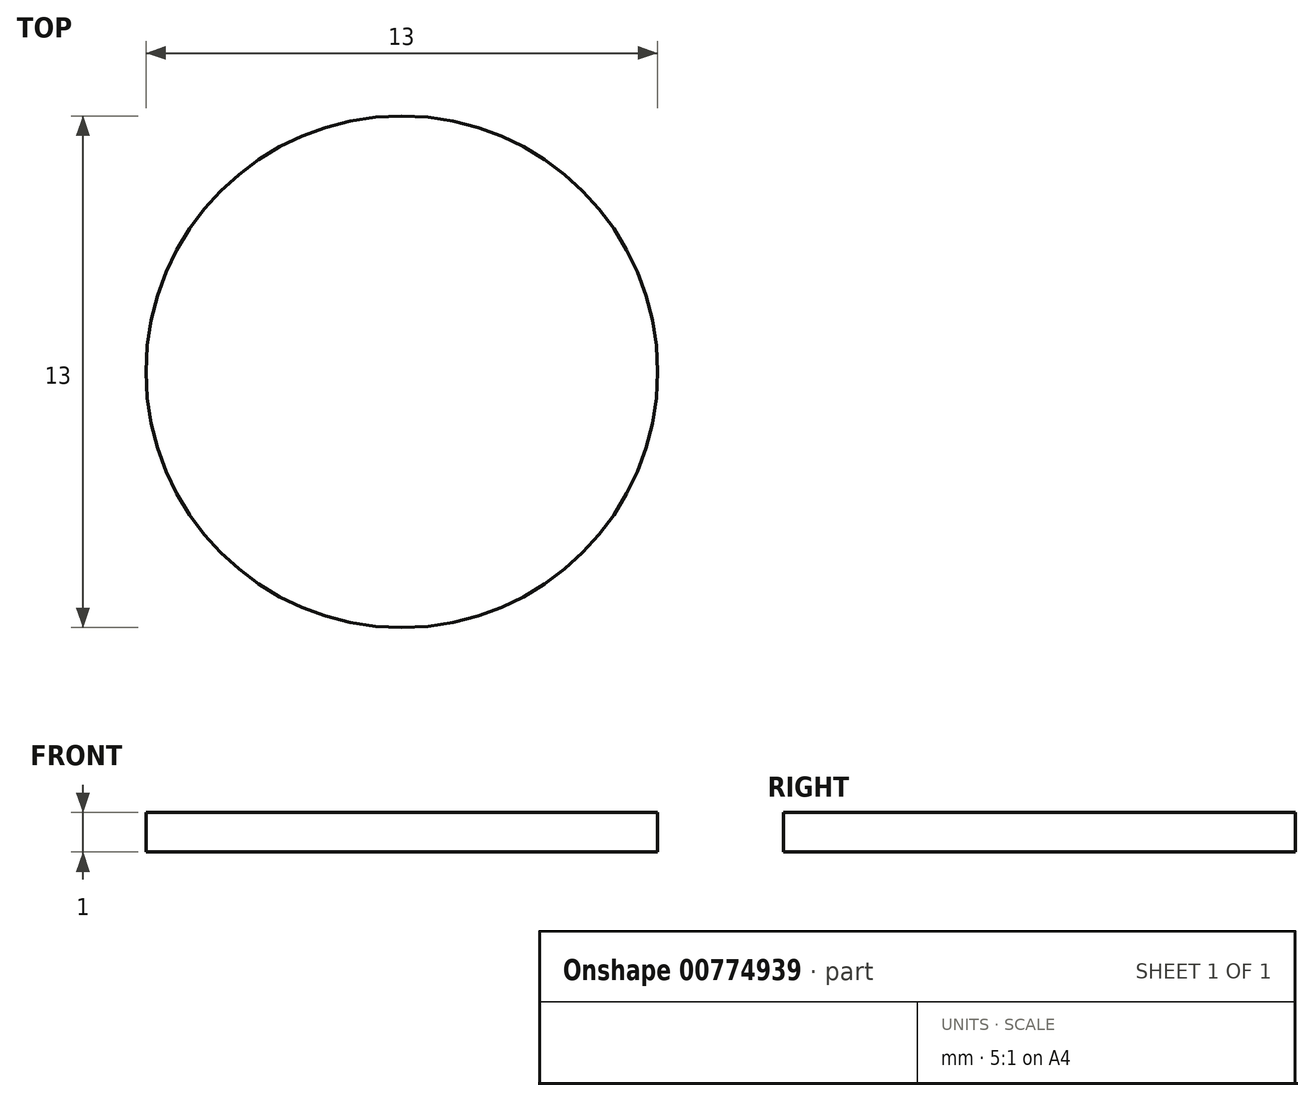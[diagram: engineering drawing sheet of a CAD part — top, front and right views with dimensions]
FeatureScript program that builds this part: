
annotation { "Feature Type Name" : "Feature", "Feature Type Description" : "" }
export const myFeature = defineFeature(function(context is Context, id is Id, definition is map)
    precondition{}
    {
        {
            var Q0;
            Q0=qCreatedBy(makeId("Top.planeOp"),FACE);
            var sketch = newSketch(context, id + "F0", { "sketchPlane" : qUnion([Q0])});
            skCircle(sketch, "E0", {"center": v(0, 0) * mm, "radius": 6.5 * mm});
            skSolve(sketch);
        }
        {
            var Q0;
            Q0 = qSketchRegion(id + "F0", true);
            extrude(context, id + "F1", {"entities" : qUnion([Q0]), "depth" : 1 * mm, "offsetDistance" : 25 * mm});
        }
    });
